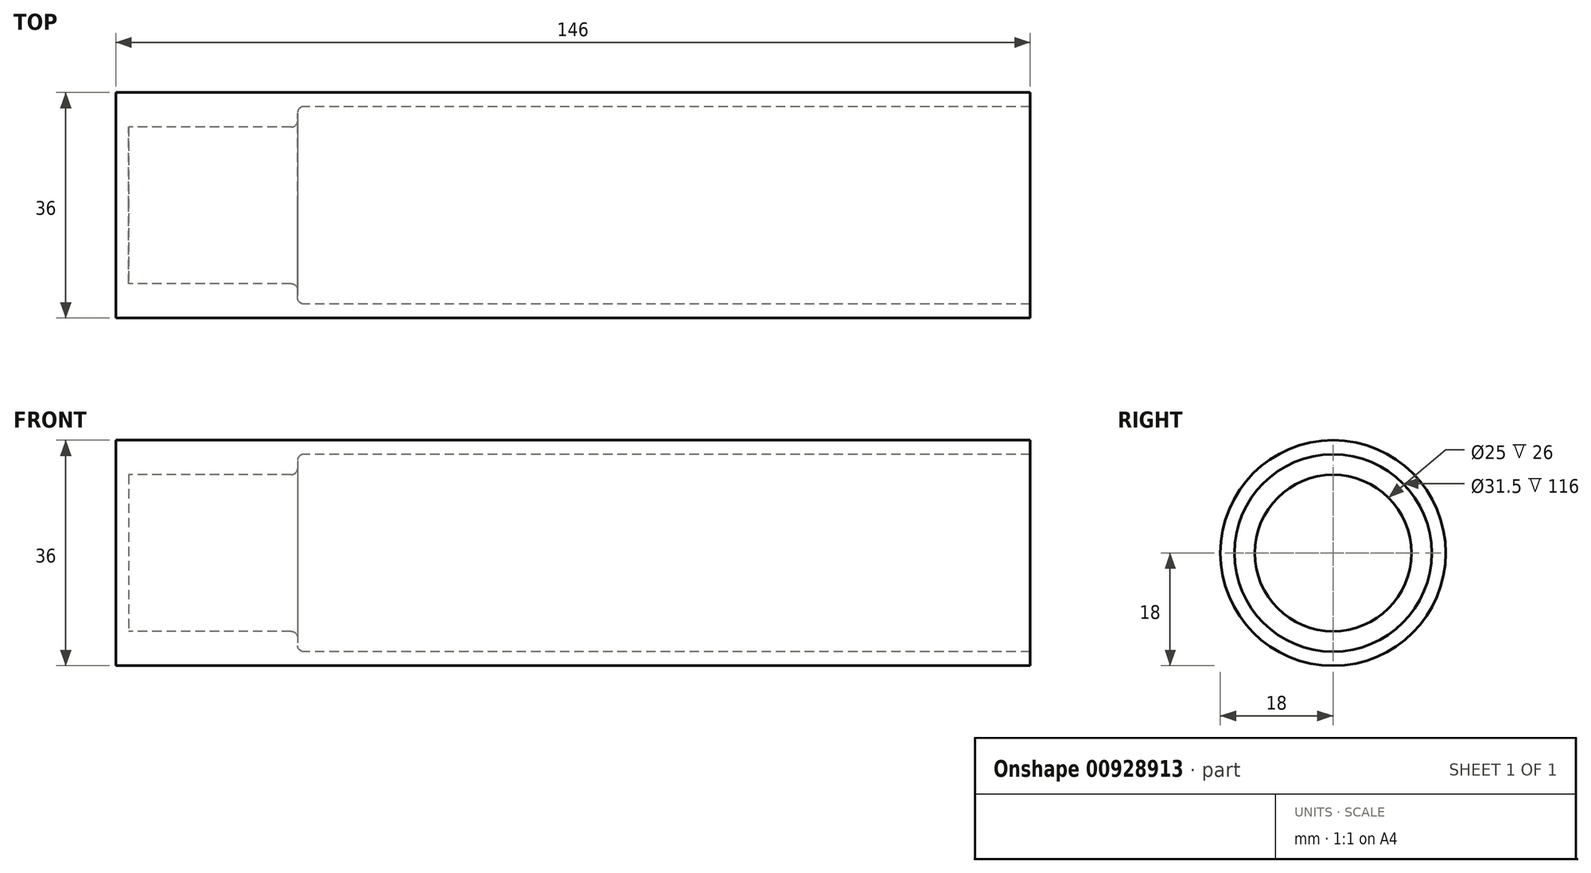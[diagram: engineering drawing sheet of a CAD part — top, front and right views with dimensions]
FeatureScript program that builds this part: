
annotation { "Feature Type Name" : "Feature", "Feature Type Description" : "" }
export const myFeature = defineFeature(function(context is Context, id is Id, definition is map)
    precondition{}
    {
        {
            var Q0;
            Q0=qCreatedBy(makeId("Front.planeOp"),FACE);
            var sketch = newSketch(context, id + "F0", { "sketchPlane" : qUnion([Q0])});
            skLineSegment(sketch, "E0", {"start": v(27, 14.75) * mm, "end": v(27, 13.5) * mm});
            skLineSegment(sketch, "E1", {"start": v(26, 12.5) * mm, "end": v(0, 12.5) * mm});
            skLineSegment(sketch, "E2", {"start": v(0, 12.5) * mm, "end": v(0, 0) * mm});
            skPoint(sketch, "E3.visualSharp", {"position": v(27, 12.5) * mm});
            skArc(sketch, "E3.filletArc", {"start": v(26, 12.5) * mm, "mid": v(26.7, 12.8) * mm, "end": v(27, 13.5) * mm});
            skPoint(sketch, "E4.visualSharp", {"position": v(27, 16) * mm});
            skLineSegment(sketch, "E5", {"start": v(0, 0) * mm, "end": v(86.5, 0) * mm});
            skLineSegment(sketch, "E6", {"start": v(0, 0) * mm, "end": v(-2, 0) * mm});
            skLineSegment(sketch, "E7", {"start": v(-2, 0) * mm, "end": v(-2, 18) * mm});
            skLineSegment(sketch, "E8", {"start": v(-2, 18) * mm, "end": v(144, 18) * mm});
            skLineSegment(sketch, "E9", {"start": v(144, 18) * mm, "end": v(144, 15.75) * mm});
            skLineSegment(sketch, "E10", {"start": v(144, 15.75) * mm, "end": v(28, 15.75) * mm});
            skPoint(sketch, "E11.visualSharp", {"position": v(27, 15.75) * mm});
            skArc(sketch, "E11.filletArc", {"start": v(28, 15.75) * mm, "mid": v(27.3, 15.46) * mm, "end": v(27, 14.75) * mm});
            skSolve(sketch);
        }
        {
            var Q0;
            Q0=makeQuery(id+"F0.imprint","IMPRINT",FACE,{"disambiguationData":[TD([[makeQuery(id+"F0.imprint","IMPRINT",EDGE,{"derivedFrom":sQuery(id+"F0.wireOp",EDGE,"E0")}),-1.0]])]});
            var Q1;
            Q1=sQuery(id+"F0.wireOp",EDGE,"E5");
            revolve(context, id + "F1", {"surfaceOperationType" : NewSurfaceOperationType.NEW, "entities" : qUnion([Q0]), "axis" : qUnion([Q1]), "revolveType" : RevolveType.FULL});
        }
    });
